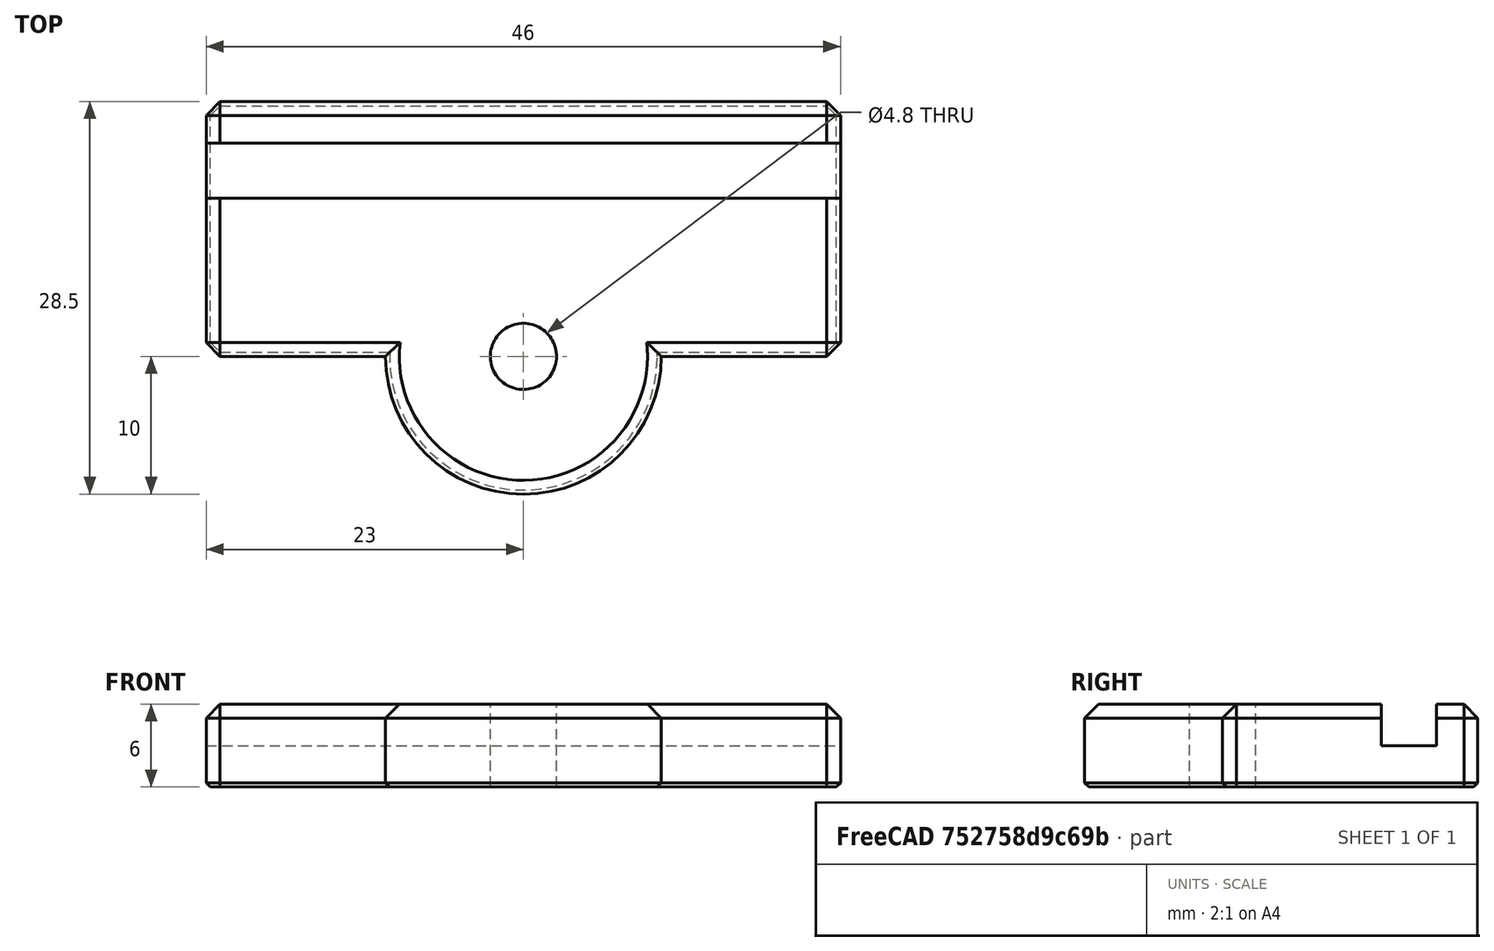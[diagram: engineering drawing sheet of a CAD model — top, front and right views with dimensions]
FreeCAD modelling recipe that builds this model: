
FCSTD DOCUMENT  (FreeCAD 0.14R3702 (Git))
Label: halterung_schanier
License: CC-BY 3.0
LicenseURL: http://creativecommons.org/licenses/by/3.0/
objects: Part::Box×2, Part::Cylinder×2, Part::Chamfer×2, Part::Cut×2, Part::MultiFuse×1
note: 9 computed .brp shape members not serialized (recipe doc carries the construction recipe); baked Part::Feature solids carry a one-line shape summary decoded from their .brp

FEATURE [Part::Box] Box  label="Cube"
  Height = 6
  Length = 46
  Placement = pos=(-23,0,0) rot=(0,0,1;0rad)
  Width = 18.5
FEATURE [Part::Cylinder] Cylinder  label="Zylinder"
  Angle = 360
  Height = 6
  Radius = 10
FEATURE [Part::Cylinder] Cylinder001  label="Zylinder001"
  Angle = 360
  Height = 10
  Placement = pos=(0,0,-2) rot=(0,0,1;0rad)
  Radius = 2.4
FEATURE [Part::Box] Box001  label="Cube001"
  Height = 10
  Length = 50
  Placement = pos=(-25,11.5,3) rot=(0,0,1;0rad)
  Width = 4
FEATURE [Part::Chamfer] Chamfer
  Base = -> Box
  Edges = 12 edges: [Edge1 r=1,Edge2 r=1,Edge3 r=1,Edge4 r=0.3,Edge5 r=1,Edge6 r=1,Edge7 r=1,Edge8 r=0.3,Edge9 r=0.3,Edge10 r=1,Edge11 r=0.3,Edge12 r=1]
FEATURE [Part::Chamfer] Chamfer001
  Base = -> Cylinder
  Edges = 2 edges: [Edge1 r=1,Edge3 r=0.3]
FEATURE [Part::MultiFuse] Fusion
  Shapes = -> [Chamfer001,Chamfer]
FEATURE [Part::Cut] Cut
  Base = -> Fusion
  Tool = -> Cylinder001
FEATURE [Part::Cut] Cut001
  Base = -> Cut
  Tool = -> Box001
